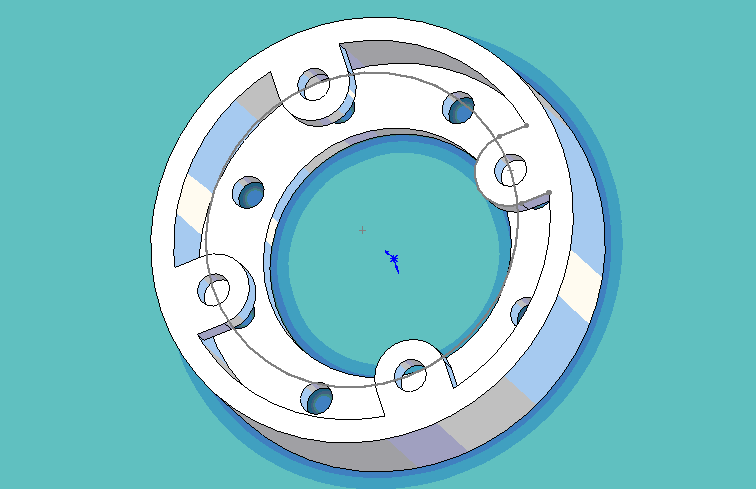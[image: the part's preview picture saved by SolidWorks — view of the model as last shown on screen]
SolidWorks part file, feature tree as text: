
SOLIDWORKS PART (.sldprt)
format: sldprt  version: not decoded by parser v0  size: 140,288 bytes
history: native  units: mm
features: sketch x5, plane x3, extrude x2, cut_extrude x2, pattern_circular x2, material x1 (+10 scaffold rows collapsed)
feature tree (25):
  scaffold x10  (default folders/planes/origin — collapsed)
  material  "Material <not specified>"
  plane  "Frontal"
  plane  "Horizontal"
  plane  "Profile"
  sketch  "Sketch1"  dims[D1=~55.339936mm]
  extrude  "Extrude1"  Depth=38.1mm
  sketch  "Sketch2"  dims[D1=~63.547976mm]
  cut_extrude  "Cut-Extrude1"  Depth=30.1625mm
  sketch  "Sketch3"  dims[D1=11.1125mm]
  cut_extrude  "Cut-Extrude2"  Depth=30.1625mm
  pattern_circular  "CirPattern1"  Count=8 Angle=360deg
  sketch  "Sketch4"  dims[D1=107.95mm]
  sketch  "Sketch5"  dims[D1=11.1125mm]
  extrude  "Extrude2"  Depth=7.9375mm
  pattern_circular  "CirPattern2"  Count=4 Angle=360deg
decode coverage: 11 of 11 modeling features carry decoded parameters
note: ~ marks probable driven/reference dimensions
note: suppression state not decoded; provenance and decode notes live in map.json
